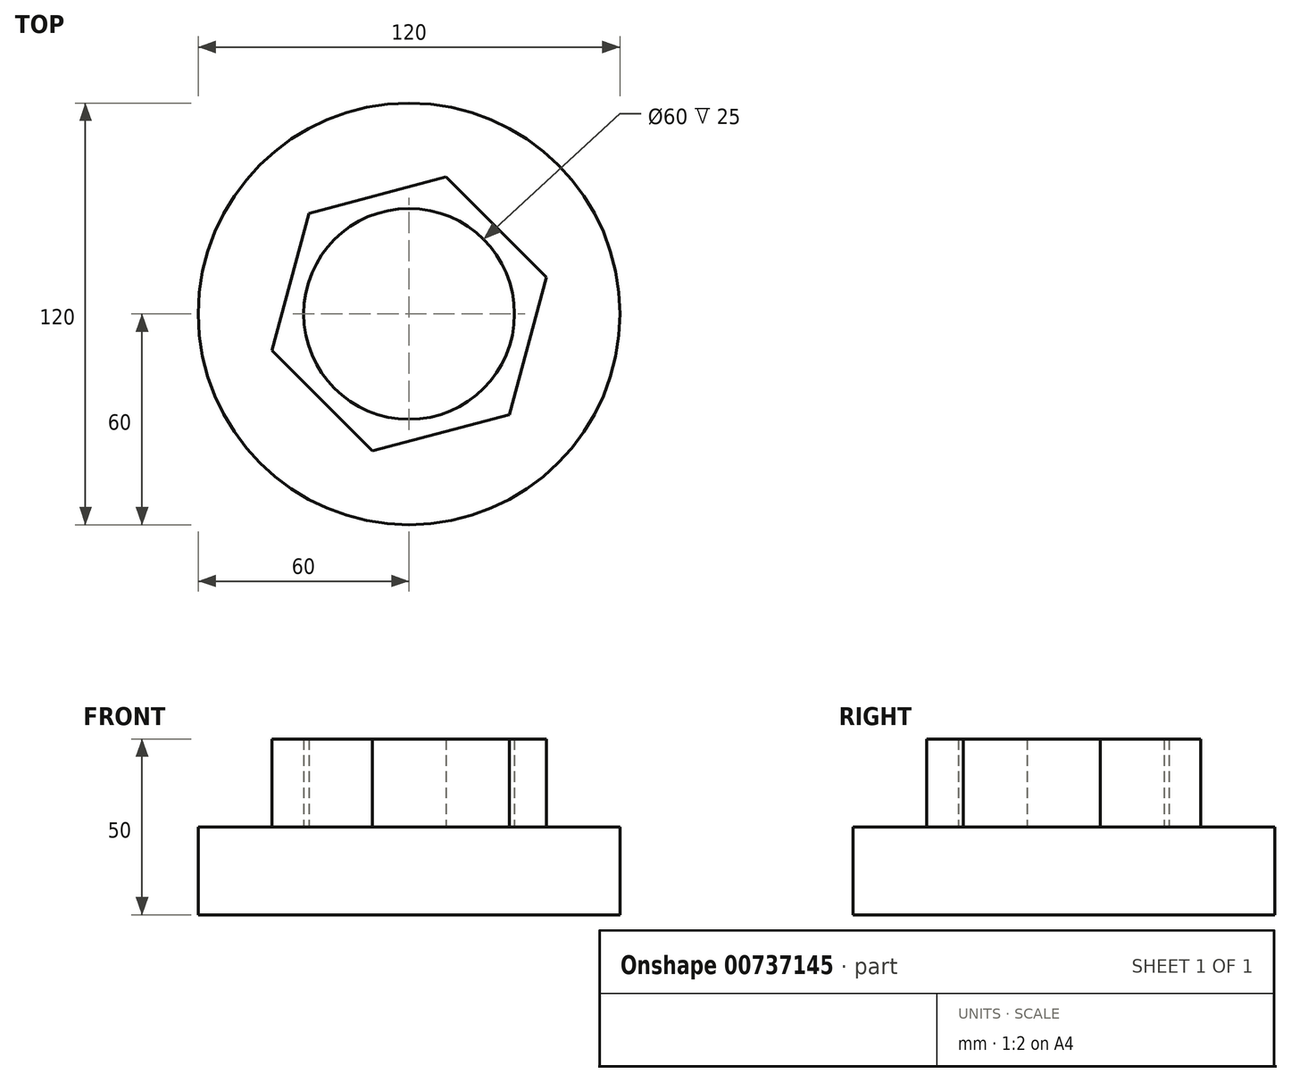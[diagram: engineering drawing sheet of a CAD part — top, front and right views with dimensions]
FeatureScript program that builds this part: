
annotation { "Feature Type Name" : "Feature", "Feature Type Description" : "" }
export const myFeature = defineFeature(function(context is Context, id is Id, definition is map)
    precondition{}
    {
        {
            var Q0;
            Q0=qCreatedBy(makeId("Top.planeOp"),FACE);
            var sketch = newSketch(context, id + "F0", { "sketchPlane" : qUnion([Q0])});
            skCircle(sketch, "E0", {"center": v(0, 0) * mm, "radius": 60 * mm});
            skSolve(sketch);
        }
        {
            var Q0;
            Q0=makeQuery(id+"F0.imprint","IMPRINT",FACE,{"disambiguationData":[TD([[makeQuery(id+"F0.imprint","IMPRINT",EDGE,{"derivedFrom":sQuery(id+"F0.wireOp",EDGE,"E0")}),1.0]])]});
            extrude(context, id + "F1", {"entities" : qUnion([Q0]), "depth" : 25 * mm, "offsetDistance" : 25 * mm});
        }
        {
            var Q0;
            Q0=makeQuery(id+"F1.opExtrude","CAP_FACE",FACE,{"disambiguationData":[OSD([sQuery(id+"F0.wireOp",EDGE,"E0")])],"isStart":false});
            var sketch = newSketch(context, id + "F2", { "sketchPlane" : qUnion([Q0])});
            skCircle(sketch, "E1.cCircle", {"center": v(0, 0) * mm, "radius": 35 * mm, "construction": true});
            skLineSegment(sketch, "E1.0", {"start": v(-28.54, 28.62) * mm, "end": v(10.52, 39.02) * mm});
            skLineSegment(sketch, "E1.1", {"start": v(10.52, 39.02) * mm, "end": v(39.05, 10.4) * mm});
            skLineSegment(sketch, "E1.2", {"start": v(39.05, 10.4) * mm, "end": v(28.54, -28.62) * mm});
            skLineSegment(sketch, "E1.3", {"start": v(28.54, -28.62) * mm, "end": v(-10.52, -39.02) * mm});
            skLineSegment(sketch, "E1.4", {"start": v(-10.52, -39.02) * mm, "end": v(-39.05, -10.4) * mm});
            skLineSegment(sketch, "E1.5", {"start": v(-39.05, -10.4) * mm, "end": v(-28.54, 28.62) * mm});
            skPoint(sketch, "E1.0.midPoint", {"position": v(-9, 33.82) * mm});
            skCircle(sketch, "E2", {"center": v(0, 0) * mm, "radius": 30 * mm});
            skSolve(sketch);
        }
        {
            var Q0;
            Q0 = qSketchRegion(id + "F2", true);
            extrude(context, id + "F3", {"entities" : qUnion([Q0]), "operationType" : NewBodyOperationType.ADD, "depth" : 25 * mm, "offsetDistance" : 25 * mm});
        }
    });
